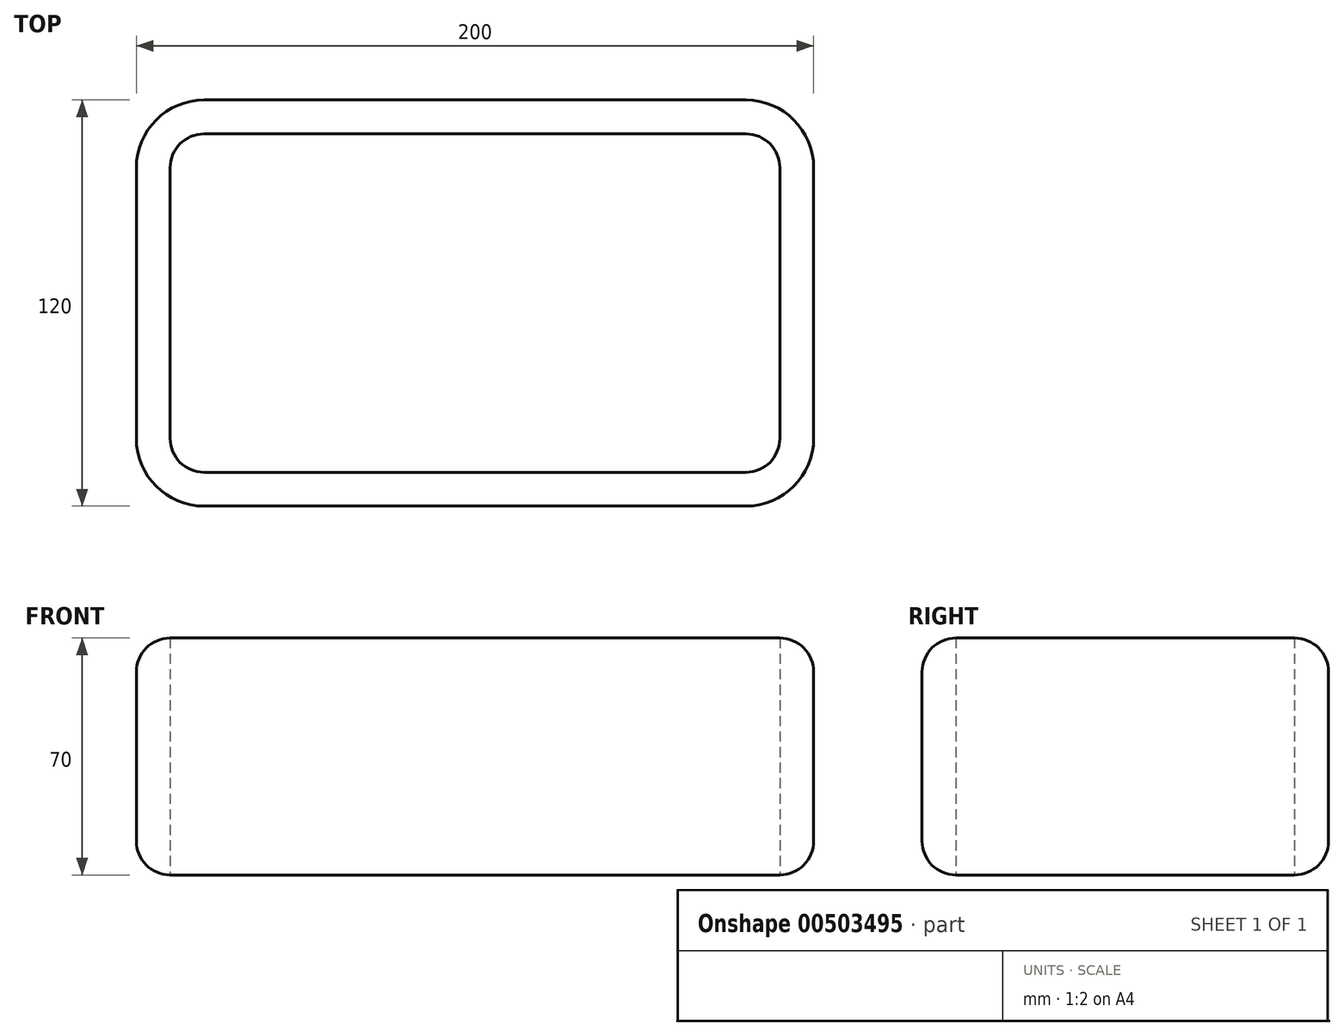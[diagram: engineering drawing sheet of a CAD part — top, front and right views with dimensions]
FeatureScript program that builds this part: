
annotation { "Feature Type Name" : "Feature", "Feature Type Description" : "" }
export const myFeature = defineFeature(function(context is Context, id is Id, definition is map)
    precondition{}
    {
        {
            var Q0;
            Q0=qCreatedBy(makeId("Top.planeOp"),FACE);
            var sketch = newSketch(context, id + "F0", { "sketchPlane" : qUnion([Q0])});
            skPoint(sketch, "E0.middle", {"position": v(0, 0) * mm});
            skLineSegment(sketch, "E1.bottom", {"start": v(-80, 60) * mm, "end": v(80, 60) * mm});
            skLineSegment(sketch, "E1.top", {"start": v(-80, -60) * mm, "end": v(80, -60) * mm});
            skLineSegment(sketch, "E1.left", {"start": v(-100, 40) * mm, "end": v(-100, -40) * mm});
            skLineSegment(sketch, "E1.right", {"start": v(100, 40) * mm, "end": v(100, -40) * mm});
            skPoint(sketch, "E2.visualSharp", {"position": v(100, 60) * mm});
            skArc(sketch, "E2.filletArc", {"start": v(100, 40) * mm, "mid": v(94.14, 54.14) * mm, "end": v(80, 60) * mm});
            skPoint(sketch, "E3.visualSharp", {"position": v(-100, 60) * mm});
            skArc(sketch, "E3.filletArc", {"start": v(-80, 60) * mm, "mid": v(-94.14, 54.14) * mm, "end": v(-100, 40) * mm});
            skPoint(sketch, "E4.visualSharp", {"position": v(-100, -60) * mm});
            skArc(sketch, "E4.filletArc", {"start": v(-100, -40) * mm, "mid": v(-94.14, -54.14) * mm, "end": v(-80, -60) * mm});
            skPoint(sketch, "E5.visualSharp", {"position": v(100, -60) * mm});
            skArc(sketch, "E5.filletArc", {"start": v(80, -60) * mm, "mid": v(94.14, -54.14) * mm, "end": v(100, -40) * mm});
            skLineSegment(sketch, "E6.0", {"start": v(-90, 40) * mm, "end": v(-90, -40) * mm});
            skArc(sketch, "E6.1", {"start": v(-80, 50) * mm, "mid": v(-87.07, 47.07) * mm, "end": v(-90, 40) * mm});
            skArc(sketch, "E6.2", {"start": v(-90, -40) * mm, "mid": v(-87.07, -47.07) * mm, "end": v(-80, -50) * mm});
            skLineSegment(sketch, "E6.3", {"start": v(-80, 50) * mm, "end": v(80, 50) * mm});
            skLineSegment(sketch, "E6.4", {"start": v(-80, -50) * mm, "end": v(80, -50) * mm});
            skArc(sketch, "E6.5", {"start": v(80, -50) * mm, "mid": v(87.07, -47.07) * mm, "end": v(90, -40) * mm});
            skLineSegment(sketch, "E6.6", {"start": v(90, 40) * mm, "end": v(90, -40) * mm});
            skArc(sketch, "E6.7", {"start": v(90, 40) * mm, "mid": v(87.07, 47.07) * mm, "end": v(80, 50) * mm});
            skSolve(sketch);
        }
        {
            var Q0;
            Q0=makeQuery(id+"F0.imprint","IMPRINT",FACE,{"disambiguationData":[TD([[makeQuery(id+"F0.imprint","IMPRINT",EDGE,{"derivedFrom":sQuery(id+"F0.wireOp",EDGE,"E1.bottom")}),-1.0]])]});
            extrude(context, id + "F1", {"entities" : qUnion([Q0]), "endBound" : BoundingType.SYMMETRIC, "depth" : 70 * mm});
        }
        {
            var Q0;
            Q0=makeQuery(id+"F1.opExtrude","CAP_EDGE",EDGE,{"disambiguationData":[OSD([sQuery(id+"F0.wireOp",EDGE,"E1.bottom")])],"isStart":false});
            var Q1;
            Q1=makeQuery(id+"F1.opExtrude","CAP_EDGE",EDGE,{"disambiguationData":[OSD([sQuery(id+"F0.wireOp",EDGE,"E1.top")])],"isStart":false});
            var Q2;
            Q2=makeQuery(id+"F1.opExtrude","CAP_EDGE",EDGE,{"disambiguationData":[OSD([sQuery(id+"F0.wireOp",EDGE,"E1.top")])],"isStart":true});
            var Q3;
            Q3=makeQuery(id+"F1.opExtrude","CAP_EDGE",EDGE,{"disambiguationData":[OSD([sQuery(id+"F0.wireOp",EDGE,"E1.bottom")])],"isStart":true});
            var Q4;
            Q4=makeQuery(id+"F1.opExtrude","CAP_EDGE",EDGE,{"disambiguationData":[OSD([sQuery(id+"F0.wireOp",EDGE,"E1.right")])],"isStart":false});
            var Q5;
            Q5=makeQuery(id+"F1.opExtrude","CAP_EDGE",EDGE,{"disambiguationData":[OSD([sQuery(id+"F0.wireOp",EDGE,"E1.right")])],"isStart":true});
            var Q6;
            Q6=makeQuery(id+"F1.opExtrude","CAP_EDGE",EDGE,{"disambiguationData":[OSD([sQuery(id+"F0.wireOp",EDGE,"E1.left")])],"isStart":true});
            var Q7;
            Q7=makeQuery(id+"F1.opExtrude","CAP_EDGE",EDGE,{"disambiguationData":[OSD([sQuery(id+"F0.wireOp",EDGE,"E1.left")])],"isStart":false});
            fillet(context, id + "F2", {"entities" : qUnion([Q0, Q1, Q2, Q3, Q4, Q5, Q6, Q7]), "radius" : 10 * mm, "allowEdgeOverflow" : false});
        }
    });
